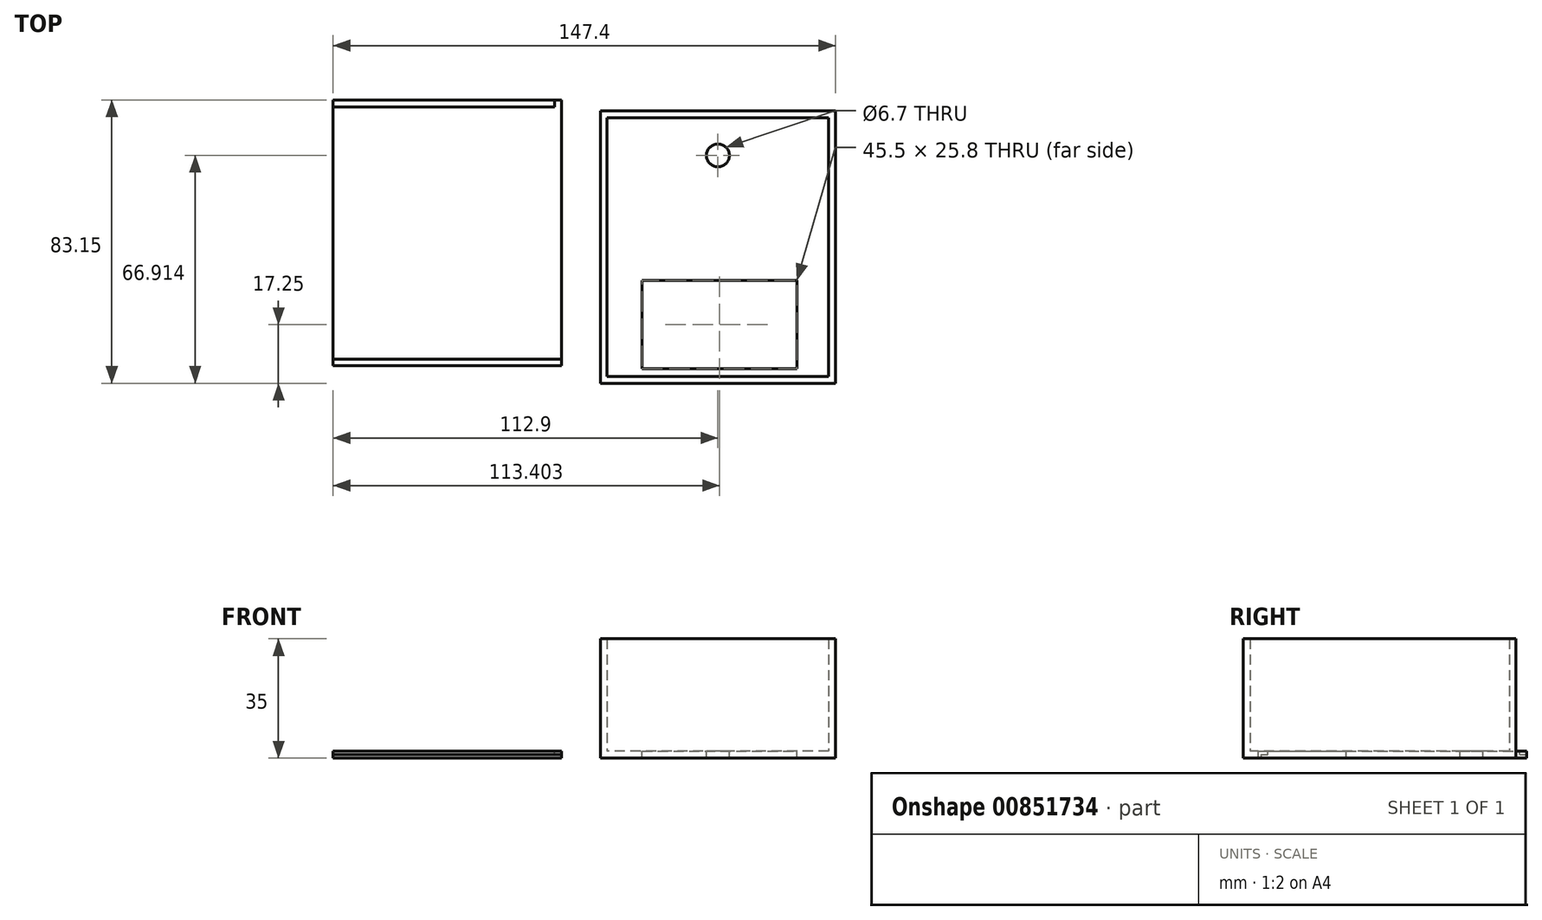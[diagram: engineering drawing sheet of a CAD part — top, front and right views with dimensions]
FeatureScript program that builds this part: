
annotation { "Feature Type Name" : "Feature", "Feature Type Description" : "" }
export const myFeature = defineFeature(function(context is Context, id is Id, definition is map)
    precondition{}
    {
        {
            var Q0;
            Q0=qCreatedBy(makeId("Top.planeOp"),FACE);
            var sketch = newSketch(context, id + "F0", { "sketchPlane" : qUnion([Q0])});
            skLineSegment(sketch, "E0.bottom", {"start": v(34.5, -40) * mm, "end": v(-34.5, -40) * mm});
            skLineSegment(sketch, "E0.top", {"start": v(34.5, 40) * mm, "end": v(-34.5, 40) * mm});
            skLineSegment(sketch, "E0.left", {"start": v(34.5, -40) * mm, "end": v(34.5, 40) * mm});
            skLineSegment(sketch, "E0.right", {"start": v(-34.5, -40) * mm, "end": v(-34.5, 40) * mm});
            skPoint(sketch, "E0.middle", {"position": v(0, 0) * mm});
            skSolve(sketch);
        }
        {
            var Q0;
            Q0=makeQuery(id+"F0.imprint","IMPRINT",FACE,{"disambiguationData":[TD([[makeQuery(id+"F0.imprint","IMPRINT",EDGE,{"derivedFrom":sQuery(id+"F0.wireOp",EDGE,"E0.bottom")}),-1.0]])]});
            extrude(context, id + "F1", {"entities" : qUnion([Q0]), "depth" : 2 * mm, "offsetDistance" : 25 * mm});
        }
        {
            var Q0;
            Q0=makeQuery(id+"F1.opExtrude","CAP_FACE",FACE,{"disambiguationData":[OSD([sQuery(id+"F0.wireOp",EDGE,"E0.bottom"),sQuery(id+"F0.wireOp",EDGE,"E0.top"),sQuery(id+"F0.wireOp",EDGE,"E0.left"),sQuery(id+"F0.wireOp",EDGE,"E0.right")])],"isStart":false});
            var sketch = newSketch(context, id + "F2", { "sketchPlane" : qUnion([Q0])});
            skLineSegment(sketch, "E1.bottom", {"start": v(34.5, 40) * mm, "end": v(-34.5, 40) * mm});
            skLineSegment(sketch, "E1.top", {"start": v(34.5, 38) * mm, "end": v(-34.5, 38) * mm});
            skLineSegment(sketch, "E1.left", {"start": v(34.5, 40) * mm, "end": v(34.5, 38) * mm});
            skLineSegment(sketch, "E1.right", {"start": v(-34.5, 40) * mm, "end": v(-34.5, 38) * mm});
            skSolve(sketch);
        }
        {
            var Q0;
            Q0=makeQuery(id+"F2.imprint","IMPRINT",FACE,{"disambiguationData":[TD([[makeQuery(id+"F2.imprint","IMPRINT",EDGE,{"derivedFrom":sQuery(id+"F2.wireOp",EDGE,"E1.bottom")}),1.0]])]});
            extrude(context, id + "F3", {"entities" : qUnion([Q0]), "operationType" : NewBodyOperationType.ADD, "depth" : 33 * mm, "offsetDistance" : 25 * mm});
        }
        {
            var Q0;
            Q0=makeQuery(id+"F1.opExtrude","CAP_FACE",FACE,{"disambiguationData":[OSD([sQuery(id+"F0.wireOp",EDGE,"E0.bottom"),sQuery(id+"F0.wireOp",EDGE,"E0.top"),sQuery(id+"F0.wireOp",EDGE,"E0.left"),sQuery(id+"F0.wireOp",EDGE,"E0.right")])],"isStart":false});
            var sketch = newSketch(context, id + "F4", { "sketchPlane" : qUnion([Q0])});
            skLineSegment(sketch, "E2.bottom", {"start": v(-34.5, 38) * mm, "end": v(-32.5, 38) * mm});
            skLineSegment(sketch, "E2.top", {"start": v(-34.5, -40) * mm, "end": v(-32.5, -40) * mm});
            skLineSegment(sketch, "E2.left", {"start": v(-34.5, 38) * mm, "end": v(-34.5, -40) * mm});
            skLineSegment(sketch, "E2.right", {"start": v(-32.5, 38) * mm, "end": v(-32.5, -40) * mm});
            skSolve(sketch);
        }
        {
            var Q0;
            Q0=makeQuery(id+"F4.imprint","IMPRINT",FACE,{"disambiguationData":[TD([[makeQuery(id+"F4.imprint","IMPRINT",EDGE,{"derivedFrom":sQuery(id+"F4.wireOp",EDGE,"E2.bottom")}),1.0]])]});
            extrude(context, id + "F5", {"entities" : qUnion([Q0]), "operationType" : NewBodyOperationType.ADD, "depth" : 33 * mm, "offsetDistance" : 25 * mm});
        }
        {
            var Q0;
            Q0=makeQuery(id+"F1.opExtrude","CAP_FACE",FACE,{"disambiguationData":[OSD([sQuery(id+"F0.wireOp",EDGE,"E0.bottom"),sQuery(id+"F0.wireOp",EDGE,"E0.top"),sQuery(id+"F0.wireOp",EDGE,"E0.left"),sQuery(id+"F0.wireOp",EDGE,"E0.right")])],"isStart":false});
            var sketch = newSketch(context, id + "F6", { "sketchPlane" : qUnion([Q0])});
            skLineSegment(sketch, "E3.bottom", {"start": v(34.5, 38) * mm, "end": v(32.5, 38) * mm});
            skLineSegment(sketch, "E3.top", {"start": v(34.5, -40) * mm, "end": v(32.5, -40) * mm});
            skLineSegment(sketch, "E3.left", {"start": v(34.5, 38) * mm, "end": v(34.5, -40) * mm});
            skLineSegment(sketch, "E3.right", {"start": v(32.5, 38) * mm, "end": v(32.5, -40) * mm});
            skSolve(sketch);
        }
        {
            var Q0;
            Q0=makeQuery(id+"F6.imprint","IMPRINT",FACE,{"disambiguationData":[TD([[makeQuery(id+"F6.imprint","IMPRINT",EDGE,{"derivedFrom":sQuery(id+"F6.wireOp",EDGE,"E3.bottom")}),1.0]])]});
            extrude(context, id + "F7", {"entities" : qUnion([Q0]), "operationType" : NewBodyOperationType.ADD, "depth" : 33 * mm, "offsetDistance" : 25 * mm});
        }
        {
            var Q0;
            Q0=makeQuery(id+"F1.opExtrude","CAP_FACE",FACE,{"disambiguationData":[OSD([sQuery(id+"F0.wireOp",EDGE,"E0.bottom"),sQuery(id+"F0.wireOp",EDGE,"E0.top"),sQuery(id+"F0.wireOp",EDGE,"E0.left"),sQuery(id+"F0.wireOp",EDGE,"E0.right")])],"isStart":false});
            var sketch = newSketch(context, id + "F8", { "sketchPlane" : qUnion([Q0])});
            skLineSegment(sketch, "E4.bottom", {"start": v(32.5, -40) * mm, "end": v(-32.5, -40) * mm});
            skLineSegment(sketch, "E4.top", {"start": v(32.5, -38) * mm, "end": v(-32.5, -38) * mm});
            skLineSegment(sketch, "E4.left", {"start": v(32.5, -40) * mm, "end": v(32.5, -38) * mm});
            skLineSegment(sketch, "E4.right", {"start": v(-32.5, -40) * mm, "end": v(-32.5, -38) * mm});
            skSolve(sketch);
        }
        {
            var Q0;
            Q0=makeQuery(id+"F8.imprint","IMPRINT",FACE,{"disambiguationData":[TD([[makeQuery(id+"F8.imprint","IMPRINT",EDGE,{"derivedFrom":sQuery(id+"F8.wireOp",EDGE,"E4.bottom")}),-1.0]])]});
            extrude(context, id + "F9", {"entities" : qUnion([Q0]), "operationType" : NewBodyOperationType.ADD, "depth" : 33 * mm, "offsetDistance" : 25 * mm});
        }
        {
            var Q0;
            Q0=qCreatedBy(makeId("Top.planeOp"),FACE);
            var sketch = newSketch(context, id + "F10", { "sketchPlane" : qUnion([Q0])});
            skLineSegment(sketch, "E5.bottom", {"start": v(-45.9, -34.85) * mm, "end": v(-112.9, -34.85) * mm});
            skLineSegment(sketch, "E5.top", {"start": v(-45.9, 43.15) * mm, "end": v(-112.9, 43.15) * mm});
            skLineSegment(sketch, "E5.left", {"start": v(-45.9, -34.85) * mm, "end": v(-45.9, 43.15) * mm});
            skLineSegment(sketch, "E5.right", {"start": v(-112.9, -34.85) * mm, "end": v(-112.9, 43.15) * mm});
            skSolve(sketch);
        }
        {
            var Q0;
            Q0=makeQuery(id+"F10.imprint","IMPRINT",FACE,{"disambiguationData":[TD([[makeQuery(id+"F10.imprint","IMPRINT",EDGE,{"derivedFrom":sQuery(id+"F10.wireOp",EDGE,"E5.bottom")}),-1.0]])]});
            extrude(context, id + "F11", {"entities" : qUnion([Q0]), "depth" : 2 * mm, "offsetDistance" : 25 * mm});
        }
        {
            var Q0;
            Q0=makeQuery(id+"F11.opExtrude","CAP_FACE",FACE,{"disambiguationData":[OSD([sQuery(id+"F10.wireOp",EDGE,"E5.bottom"),sQuery(id+"F10.wireOp",EDGE,"E5.top"),sQuery(id+"F10.wireOp",EDGE,"E5.left"),sQuery(id+"F10.wireOp",EDGE,"E5.right")])],"isStart":false});
            var sketch = newSketch(context, id + "F12", { "sketchPlane" : qUnion([Q0])});
            skLineSegment(sketch, "E6.bottom", {"start": v(-45.9, -34.85) * mm, "end": v(-112.9, -34.85) * mm});
            skLineSegment(sketch, "E6.top", {"start": v(-45.9, -32.85) * mm, "end": v(-112.9, -32.85) * mm});
            skLineSegment(sketch, "E6.left", {"start": v(-45.9, -34.85) * mm, "end": v(-45.9, -32.85) * mm});
            skLineSegment(sketch, "E6.right", {"start": v(-112.9, -34.85) * mm, "end": v(-112.9, -32.85) * mm});
            skLineSegment(sketch, "E7.bottom", {"start": v(-45.9, -32.85) * mm, "end": v(-47.9, -32.85) * mm});
            skLineSegment(sketch, "E7.top", {"start": v(-45.9, 43.15) * mm, "end": v(-47.9, 43.15) * mm});
            skLineSegment(sketch, "E7.left", {"start": v(-45.9, -32.85) * mm, "end": v(-45.9, 43.15) * mm});
            skLineSegment(sketch, "E7.right", {"start": v(-47.9, -32.85) * mm, "end": v(-47.9, 43.15) * mm});
            skLineSegment(sketch, "E8.bottom", {"start": v(-47.9, 43.15) * mm, "end": v(-112.9, 43.15) * mm});
            skLineSegment(sketch, "E8.top", {"start": v(-47.9, 41.15) * mm, "end": v(-112.9, 41.15) * mm});
            skLineSegment(sketch, "E8.left", {"start": v(-47.9, 43.15) * mm, "end": v(-47.9, 41.15) * mm});
            skLineSegment(sketch, "E8.right", {"start": v(-112.9, 43.15) * mm, "end": v(-112.9, 41.15) * mm});
            skLineSegment(sketch, "E9.bottom", {"start": v(-112.9, 41.15) * mm, "end": v(-110.9, 41.15) * mm});
            skLineSegment(sketch, "E9.top", {"start": v(-112.9, -32.85) * mm, "end": v(-110.9, -32.85) * mm});
            skLineSegment(sketch, "E9.left", {"start": v(-112.9, 41.15) * mm, "end": v(-112.9, -32.85) * mm});
            skLineSegment(sketch, "E9.right", {"start": v(-110.9, 41.15) * mm, "end": v(-110.9, -32.85) * mm});
            skSolve(sketch);
        }
        {
            var Q0;
            Q0=makeQuery(id+"F12.imprint","IMPRINT",FACE,{"disambiguationData":[TD([[makeQuery(id+"F12.imprint","IMPRINT",EDGE,{"derivedFrom":sQuery(id+"F12.wireOp",EDGE,"E6.bottom")}),-1.0]])]});
            var Q1;
            Q1=makeQuery(id+"F12.imprint","IMPRINT",FACE,{"disambiguationData":[TD([[makeQuery(id+"F12.imprint","IMPRINT",EDGE,{"derivedFrom":sQuery(id+"F12.wireOp",EDGE,"E9.bottom")}),-1.0]])]});
            var Q2;
            Q2=makeQuery(id+"F12.imprint","IMPRINT",FACE,{"disambiguationData":[TD([[makeQuery(id+"F12.imprint","IMPRINT",EDGE,{"derivedFrom":sQuery(id+"F12.wireOp",EDGE,"E8.bottom")}),1.0]])]});
            var Q3;
            Q3=makeQuery(id+"F12.imprint","IMPRINT",FACE,{"disambiguationData":[TD([[makeQuery(id+"F12.imprint","IMPRINT",EDGE,{"derivedFrom":sQuery(id+"F12.wireOp",EDGE,"E7.bottom")}),-1.0]])]});
            extrude(context, id + "F13", {"entities" : qUnion([Q0, Q1, Q2, Q3]), "operationType" : NewBodyOperationType.REMOVE, "oppositeDirection" : true, "depth" : 1 * mm, "offsetDistance" : 25 * mm});
        }
        {
            var Q0;
            Q0=makeQuery(id+"F1.opExtrude","CAP_FACE",FACE,{"disambiguationData":[OSD([sQuery(id+"F0.wireOp",EDGE,"E0.bottom"),sQuery(id+"F0.wireOp",EDGE,"E0.top"),sQuery(id+"F0.wireOp",EDGE,"E0.left"),sQuery(id+"F0.wireOp",EDGE,"E0.right")])],"isStart":false});
            var sketch = newSketch(context, id + "F14", { "sketchPlane" : qUnion([Q0])});
            skLineSegment(sketch, "E10.bottom", {"start": v(-22.25, -35.65) * mm, "end": v(23.25, -35.65) * mm});
            skLineSegment(sketch, "E10.top", {"start": v(-22.25, -9.85) * mm, "end": v(23.25, -9.85) * mm});
            skLineSegment(sketch, "E10.left", {"start": v(-22.25, -35.65) * mm, "end": v(-22.25, -9.85) * mm});
            skLineSegment(sketch, "E10.right", {"start": v(23.25, -35.65) * mm, "end": v(23.25, -9.85) * mm});
            skPoint(sketch, "E10.middle", {"position": v(0.5, -22.75) * mm});
            skCircle(sketch, "E11", {"center": v(0, 26.91) * mm, "radius": 3.35 * mm});
            skSolve(sketch);
        }
        {
            var Q0;
            Q0=makeQuery(id+"F14.imprint","IMPRINT",FACE,{"disambiguationData":[TD([[makeQuery(id+"F14.imprint","IMPRINT",EDGE,{"derivedFrom":sQuery(id+"F14.wireOp",EDGE,"E10.bottom")}),1.0]])]});
            var Q1;
            Q1=makeQuery(id+"F14.imprint","IMPRINT",FACE,{"disambiguationData":[TD([[makeQuery(id+"F14.imprint","IMPRINT",EDGE,{"derivedFrom":sQuery(id+"F14.wireOp",EDGE,"E11")}),1.0]])]});
            extrude(context, id + "F15", {"entities" : qUnion([Q0, Q1]), "operationType" : NewBodyOperationType.REMOVE, "endBound" : BoundingType.THROUGH_ALL, "oppositeDirection" : true, "depth" : 25 * mm, "offsetDistance" : 25 * mm});
        }
    });
